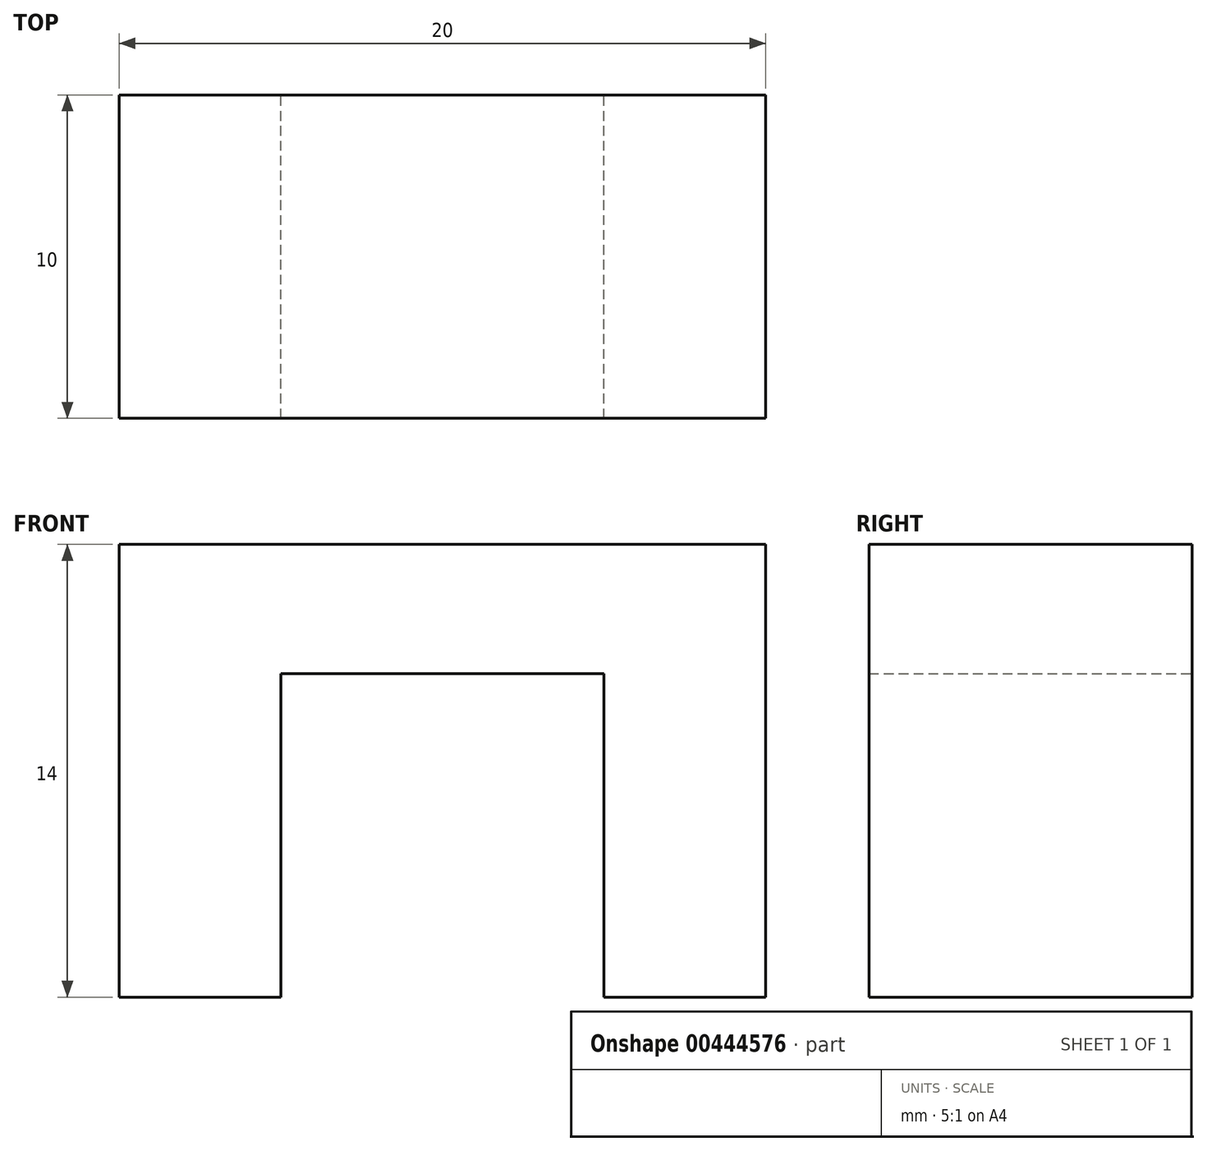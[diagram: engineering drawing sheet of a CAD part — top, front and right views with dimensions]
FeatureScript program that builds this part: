
annotation { "Feature Type Name" : "Feature", "Feature Type Description" : "" }
export const myFeature = defineFeature(function(context is Context, id is Id, definition is map)
    precondition{}
    {
        {
            var Q0;
            Q0=qCreatedBy(makeId("Front.planeOp"),FACE);
            var sketch = newSketch(context, id + "F0", { "sketchPlane" : qUnion([Q0])});
            skLineSegment(sketch, "E0.bottom", {"start": v(0, 0) * mm, "end": v(20, 0) * mm});
            skLineSegment(sketch, "E0.top", {"start": v(0, 14) * mm, "end": v(20, 14) * mm});
            skLineSegment(sketch, "E0.left", {"start": v(0, 0) * mm, "end": v(0, 14) * mm});
            skLineSegment(sketch, "E0.right", {"start": v(20, 0) * mm, "end": v(20, 14) * mm});
            skLineSegment(sketch, "E1.bottom", {"start": v(5, 0) * mm, "end": v(15, 0) * mm});
            skLineSegment(sketch, "E1.top", {"start": v(5, 10) * mm, "end": v(15, 10) * mm});
            skLineSegment(sketch, "E1.left", {"start": v(5, 0) * mm, "end": v(5, 10) * mm});
            skLineSegment(sketch, "E1.right", {"start": v(15, 0) * mm, "end": v(15, 10) * mm});
            skSolve(sketch);
        }
        {
            var Q0;
            Q0=makeQuery(id+"F0.imprint","IMPRINT",FACE,{"disambiguationData":[TD([[makeQuery(id+"F0.imprint","IMPRINT",EDGE,{"derivedFrom":sQuery(id+"F0.wireOp",EDGE,"E0.top")}),-1.0]])]});
            extrude(context, id + "F1", {"entities" : qUnion([Q0]), "depth" : 10 * mm, "offsetDistance" : 25 * mm});
        }
    });
